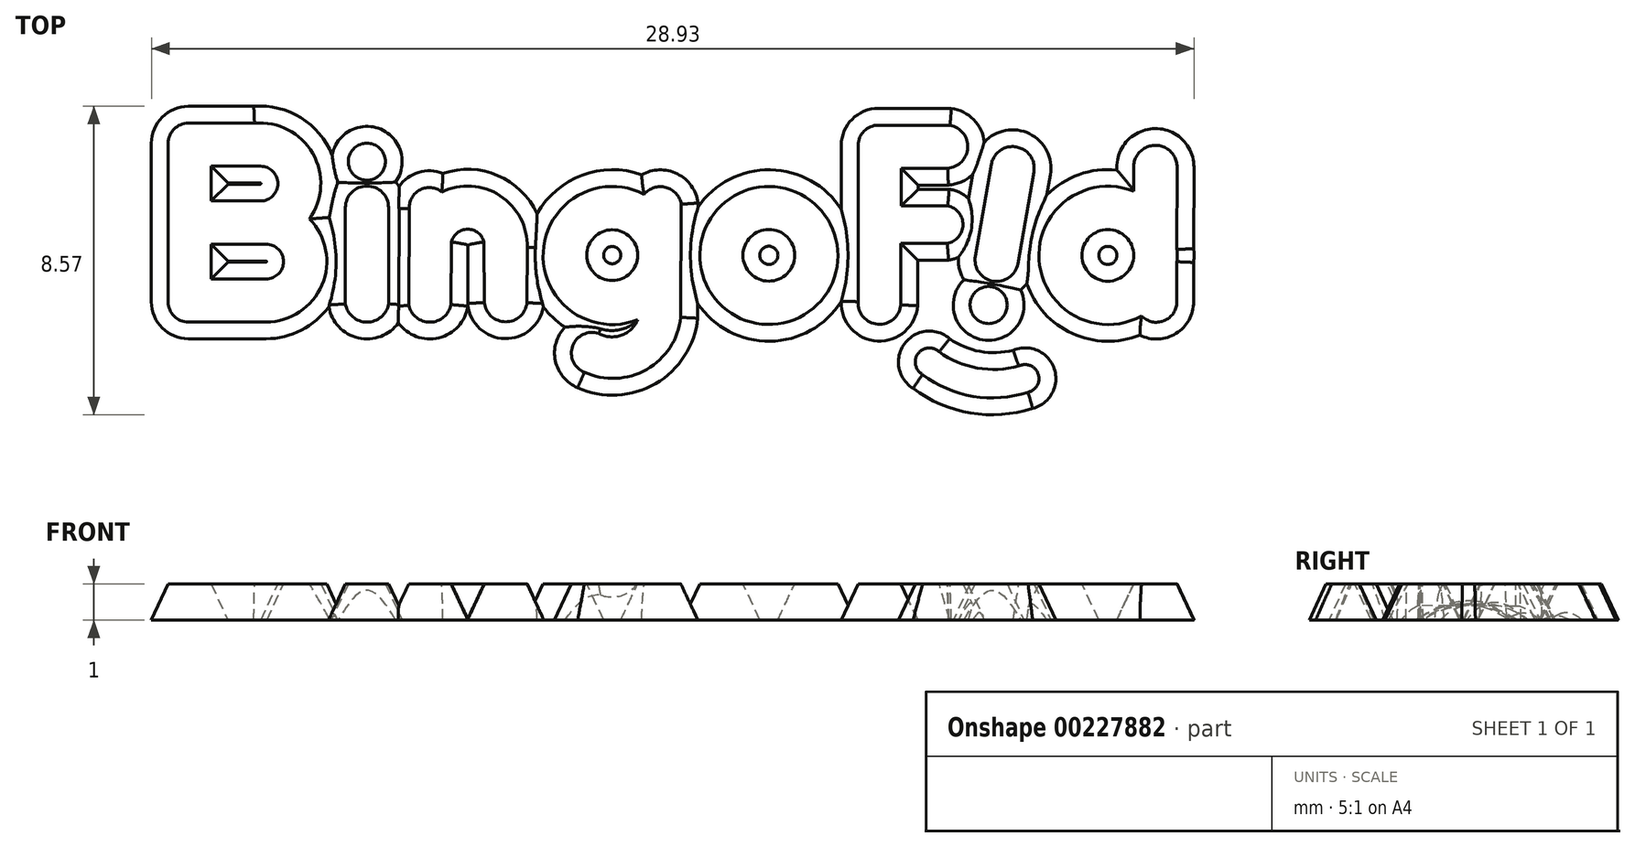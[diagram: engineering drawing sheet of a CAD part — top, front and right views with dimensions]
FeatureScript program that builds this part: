
annotation { "Feature Type Name" : "Feature", "Feature Type Description" : "" }
export const myFeature = defineFeature(function(context is Context, id is Id, definition is map)
    precondition{}
    {
        {
            var Q0;
            Q0=qCreatedBy(makeId("Top.planeOp"),FACE);
            var sketch = newSketch(context, id + "F0", { "sketchPlane" : qUnion([Q0])});
            skArc(sketch, "E0.0.0", {"start": v(-138.67, -42.82) * mm, "mid": v(-138.58, -41) * mm, "end": v(-140.2, -40.16) * mm});
            skLineSegment(sketch, "E0.0.1", {"start": v(-140.2, -40.16) * mm, "end": v(-142.04, -40.16) * mm});
            skArc(sketch, "E0.0.2", {"start": v(-142.04, -40.16) * mm, "mid": v(-142.43, -40.32) * mm, "end": v(-142.6, -40.72) * mm});
            skLineSegment(sketch, "E0.0.3", {"start": v(-142.6, -40.72) * mm, "end": v(-142.6, -45.12) * mm});
            skArc(sketch, "E0.0.4", {"start": v(-142.6, -45.12) * mm, "mid": v(-142.43, -45.52) * mm, "end": v(-142.04, -45.68) * mm});
            skLineSegment(sketch, "E0.0.5", {"start": v(-142.04, -45.68) * mm, "end": v(-139.88, -45.68) * mm});
            skArc(sketch, "E0.0.6", {"start": v(-139.88, -45.68) * mm, "mid": v(-138.33, -44.65) * mm, "end": v(-138.67, -42.82) * mm});
            skArc(sketch, "E1.0.0", {"start": v(-136.48, -42.5) * mm, "mid": v(-137.08, -41.9) * mm, "end": v(-137.68, -42.5) * mm});
            skLineSegment(sketch, "E1.0.1", {"start": v(-137.68, -42.5) * mm, "end": v(-137.68, -45.18) * mm});
            skArc(sketch, "E1.0.2", {"start": v(-137.68, -45.18) * mm, "mid": v(-137.08, -45.69) * mm, "end": v(-136.48, -45.18) * mm});
            skLineSegment(sketch, "E1.0.3", {"start": v(-136.48, -45.18) * mm, "end": v(-136.48, -42.5) * mm});
            skCircle(sketch, "E2.0.0", {"center": v(-137.08, -41.23) * mm, "radius": 0.51 * mm});
            skArc(sketch, "E3.0.0", {"start": v(-135, -42.07) * mm, "mid": v(-135.6, -42) * mm, "end": v(-135.9, -42.53) * mm});
            skLineSegment(sketch, "E3.0.1", {"start": v(-135.9, -42.53) * mm, "end": v(-135.92, -45.22) * mm});
            skArc(sketch, "E3.0.2", {"start": v(-135.92, -45.22) * mm, "mid": v(-135.33, -45.69) * mm, "end": v(-134.75, -45.2) * mm});
            skLineSegment(sketch, "E3.0.3", {"start": v(-134.75, -45.2) * mm, "end": v(-134.73, -43.46) * mm});
            skArc(sketch, "E3.0.4", {"start": v(-134.73, -43.46) * mm, "mid": v(-134.28, -43.1) * mm, "end": v(-133.83, -43.46) * mm});
            skLineSegment(sketch, "E3.0.5", {"start": v(-133.83, -43.46) * mm, "end": v(-133.82, -45.14) * mm});
            skArc(sketch, "E3.0.6", {"start": v(-133.82, -45.14) * mm, "mid": v(-133.23, -45.68) * mm, "end": v(-132.64, -45.15) * mm});
            skLineSegment(sketch, "E3.0.7", {"start": v(-132.64, -45.15) * mm, "end": v(-132.63, -43.62) * mm});
            skArc(sketch, "E3.0.8", {"start": v(-132.63, -43.62) * mm, "mid": v(-133.38, -42.18) * mm, "end": v(-135, -42.07) * mm});
            skArc(sketch, "E4.0.0", {"start": v(-128.36, -42.41) * mm, "mid": v(-128.78, -41.94) * mm, "end": v(-129.39, -42.14) * mm});
            skArc(sketch, "E4.0.1", {"start": v(-129.39, -42.14) * mm, "mid": v(-132.19, -43.74) * mm, "end": v(-129.57, -45.62) * mm});
            skArc(sketch, "E4.0.2", {"start": v(-129.57, -45.62) * mm, "mid": v(-130.02, -46.05) * mm, "end": v(-130.65, -46) * mm});
            skArc(sketch, "E4.0.3", {"start": v(-130.65, -46) * mm, "mid": v(-131.37, -46.35) * mm, "end": v(-131.05, -47.08) * mm});
            skArc(sketch, "E4.0.4", {"start": v(-131.05, -47.08) * mm, "mid": v(-129.32, -47) * mm, "end": v(-128.37, -45.55) * mm});
            skLineSegment(sketch, "E4.0.5", {"start": v(-128.37, -45.55) * mm, "end": v(-128.36, -42.41) * mm});
            skCircle(sketch, "E5.0.0", {"center": v(-125.93, -43.84) * mm, "radius": 1.92 * mm});
            skArc(sketch, "E6.0.0", {"start": v(-120.98, -43.5) * mm, "mid": v(-120.54, -42.98) * mm, "end": v(-120.96, -42.46) * mm});
            skLineSegment(sketch, "E6.0.1", {"start": v(-120.96, -42.46) * mm, "end": v(-122.26, -42.46) * mm});
            skLineSegment(sketch, "E6.0.2", {"start": v(-122.26, -42.46) * mm, "end": v(-122.26, -42.46) * mm});
            skFitSpline(sketch, "E6.0.3", {"points": [v(-122.26, -42.46) * mm, v(-122.26, -42.1) * mm, v(-122.26, -41.76) * mm, v(-122.26, -41.41) * mm]});
            skFitSpline(sketch, "E6.0.4", {"points": [v(-122.26, -41.41) * mm, v(-122.03, -41.41) * mm, v(-121.8, -41.41) * mm, v(-121.58, -41.41) * mm]});
            skLineSegment(sketch, "E6.0.5", {"start": v(-121.58, -41.41) * mm, "end": v(-120.96, -41.41) * mm});
            skArc(sketch, "E6.0.6", {"start": v(-120.96, -41.41) * mm, "mid": v(-120.4, -40.84) * mm, "end": v(-120.9, -40.22) * mm});
            skLineSegment(sketch, "E6.0.7", {"start": v(-120.9, -40.22) * mm, "end": v(-122.9, -40.22) * mm});
            skArc(sketch, "E6.0.8", {"start": v(-122.9, -40.22) * mm, "mid": v(-123.29, -40.38) * mm, "end": v(-123.45, -40.78) * mm});
            skLineSegment(sketch, "E6.0.9", {"start": v(-123.45, -40.78) * mm, "end": v(-123.45, -45.12) * mm});
            skArc(sketch, "E6.0.10", {"start": v(-123.45, -45.12) * mm, "mid": v(-122.9, -45.75) * mm, "end": v(-122.27, -45.21) * mm});
            skLineSegment(sketch, "E6.0.11", {"start": v(-122.27, -45.21) * mm, "end": v(-122.27, -43.5) * mm});
            skLineSegment(sketch, "E6.0.12", {"start": v(-122.27, -43.5) * mm, "end": v(-120.98, -43.5) * mm});
            skArc(sketch, "E7.0.0", {"start": v(-120.2, -43.86) * mm, "mid": v(-119.71, -44.55) * mm, "end": v(-119.02, -44.06) * mm});
            skLineSegment(sketch, "E7.0.1", {"start": v(-119.02, -44.06) * mm, "end": v(-118.57, -41.51) * mm});
            skArc(sketch, "E7.0.2", {"start": v(-118.57, -41.51) * mm, "mid": v(-119.06, -40.82) * mm, "end": v(-119.75, -41.3) * mm});
            skLineSegment(sketch, "E7.0.3", {"start": v(-119.75, -41.3) * mm, "end": v(-120.2, -43.86) * mm});
            skCircle(sketch, "E8.0.0", {"center": v(-119.83, -45.21) * mm, "radius": 0.52 * mm});
            skArc(sketch, "E9.0.0", {"start": v(-121.2, -46.51) * mm, "mid": v(-121.79, -46.57) * mm, "end": v(-121.66, -47.14) * mm});
            skArc(sketch, "E9.0.1", {"start": v(-121.66, -47.14) * mm, "mid": v(-120.26, -47.75) * mm, "end": v(-118.73, -47.63) * mm});
            skArc(sketch, "E9.0.2", {"start": v(-118.73, -47.63) * mm, "mid": v(-118.45, -47.13) * mm, "end": v(-119, -46.9) * mm});
            skArc(sketch, "E9.0.3", {"start": v(-119, -46.9) * mm, "mid": v(-120.14, -46.96) * mm, "end": v(-121.2, -46.51) * mm});
            skLineSegment(sketch, "E10.0.0", {"start": v(-115.8, -41.39) * mm, "end": v(-115.8, -42.05) * mm});
            skArc(sketch, "E10.0.1", {"start": v(-115.8, -42.05) * mm, "mid": v(-118.43, -43.95) * mm, "end": v(-115.59, -45.51) * mm});
            skArc(sketch, "E10.0.2", {"start": v(-115.59, -45.51) * mm, "mid": v(-114.96, -45.65) * mm, "end": v(-114.6, -45.12) * mm});
            skLineSegment(sketch, "E10.0.3", {"start": v(-114.6, -45.12) * mm, "end": v(-114.6, -44) * mm});
            skArc(sketch, "E10.0.4", {"start": v(-114.6, -44) * mm, "mid": v(-114.6, -43.84) * mm, "end": v(-114.6, -43.67) * mm});
            skLineSegment(sketch, "E10.0.5", {"start": v(-114.6, -43.67) * mm, "end": v(-114.6, -41.38) * mm});
            skArc(sketch, "E10.0.6", {"start": v(-114.6, -41.38) * mm, "mid": v(-115.2, -40.78) * mm, "end": v(-115.8, -41.39) * mm});
            skArc(sketch, "E11.0", {"start": v(-140.03, -42.32) * mm, "mid": v(-139.55, -41.84) * mm, "end": v(-140.03, -41.36) * mm});
            skFitSpline(sketch, "E12.0", {"points": [v(-141.4, -42.32) * mm, v(-141.4, -42) * mm, v(-141.4, -41.68) * mm, v(-141.4, -41.36) * mm]});
            skFitSpline(sketch, "E12.1", {"points": [v(-141.4, -44.49) * mm, v(-141.4, -44.17) * mm, v(-141.4, -43.84) * mm, v(-141.4, -43.52) * mm]});
            skArc(sketch, "E12.2", {"start": v(-139.88, -44.49) * mm, "mid": v(-139.4, -44) * mm, "end": v(-139.88, -43.52) * mm});
            skCircle(sketch, "E13.0", {"center": v(-130.27, -43.83) * mm, "radius": 0.7 * mm});
            skCircle(sketch, "E14.0", {"center": v(-125.93, -43.83) * mm, "radius": 0.72 * mm});
            skCircle(sketch, "E15.0", {"center": v(-116.52, -43.83) * mm, "radius": 0.72 * mm});
            skLineSegment(sketch, "E16", {"start": v(-141.4, -41.36) * mm, "end": v(-140.03, -41.36) * mm});
            skLineSegment(sketch, "E17", {"start": v(-141.4, -42.32) * mm, "end": v(-140.03, -42.32) * mm});
            skLineSegment(sketch, "E18", {"start": v(-141.4, -43.52) * mm, "end": v(-139.88, -43.52) * mm});
            skLineSegment(sketch, "E19", {"start": v(-141.4, -44.49) * mm, "end": v(-139.88, -44.49) * mm});
            skSolve(sketch);
        }
        {
            var Q0;
            Q0=makeQuery(id+"F0.imprint","IMPRINT",FACE,{"disambiguationData":[TD([[makeQuery(id+"F0.imprint","IMPRINT",EDGE,{"derivedFrom":sQuery(id+"F0.wireOp",EDGE,"E0.0.0")}),1.0]])]});
            var Q1;
            Q1=makeQuery(id+"F0.imprint","IMPRINT",FACE,{"disambiguationData":[TD([[makeQuery(id+"F0.imprint","IMPRINT",EDGE,{"derivedFrom":sQuery(id+"F0.wireOp",EDGE,"E1.0.0")}),1.0]])]});
            var Q2;
            Q2=makeQuery(id+"F0.imprint","IMPRINT",FACE,{"disambiguationData":[TD([[makeQuery(id+"F0.imprint","IMPRINT",EDGE,{"derivedFrom":sQuery(id+"F0.wireOp",EDGE,"E2.0.0")}),1.0]])]});
            var Q3;
            Q3=makeQuery(id+"F0.imprint","IMPRINT",FACE,{"disambiguationData":[TD([[makeQuery(id+"F0.imprint","IMPRINT",EDGE,{"derivedFrom":sQuery(id+"F0.wireOp",EDGE,"E3.0.0")}),1.0]])]});
            var Q4;
            Q4=makeQuery(id+"F0.imprint","IMPRINT",FACE,{"disambiguationData":[TD([[makeQuery(id+"F0.imprint","IMPRINT",EDGE,{"derivedFrom":sQuery(id+"F0.wireOp",EDGE,"E4.0.0")}),1.0]])]});
            var Q5;
            Q5=makeQuery(id+"F0.imprint","IMPRINT",FACE,{"disambiguationData":[TD([[makeQuery(id+"F0.imprint","IMPRINT",EDGE,{"derivedFrom":sQuery(id+"F0.wireOp",EDGE,"E5.0.0")}),1.0]])]});
            var Q6;
            Q6=makeQuery(id+"F0.imprint","IMPRINT",FACE,{"disambiguationData":[TD([[makeQuery(id+"F0.imprint","IMPRINT",EDGE,{"derivedFrom":sQuery(id+"F0.wireOp",EDGE,"E6.0.0")}),1.0]])]});
            var Q7;
            Q7=makeQuery(id+"F0.imprint","IMPRINT",FACE,{"disambiguationData":[TD([[makeQuery(id+"F0.imprint","IMPRINT",EDGE,{"derivedFrom":sQuery(id+"F0.wireOp",EDGE,"E7.0.0")}),1.0]])]});
            var Q8;
            Q8=makeQuery(id+"F0.imprint","IMPRINT",FACE,{"disambiguationData":[TD([[makeQuery(id+"F0.imprint","IMPRINT",EDGE,{"derivedFrom":sQuery(id+"F0.wireOp",EDGE,"E10.0.0")}),1.0]])]});
            var Q9;
            Q9=makeQuery(id+"F0.imprint","IMPRINT",FACE,{"disambiguationData":[TD([[makeQuery(id+"F0.imprint","IMPRINT",EDGE,{"derivedFrom":sQuery(id+"F0.wireOp",EDGE,"E8.0.0")}),1.0]])]});
            var Q10;
            Q10=makeQuery(id+"F0.imprint","IMPRINT",FACE,{"disambiguationData":[TD([[makeQuery(id+"F0.imprint","IMPRINT",EDGE,{"derivedFrom":sQuery(id+"F0.wireOp",EDGE,"E9.0.0")}),1.0]])]});
            extrude(context, id + "F1", {"entities" : qUnion([Q0, Q1, Q2, Q3, Q4, Q5, Q6, Q7, Q8, Q9, Q10]), "oppositeDirection" : true, "depth" : 1 * mm, "hasDraft" : true, "draftAngle" : 25 * degree});
        }
        {
            var Q0;
            Q0=makeQuery(id+"F1.opExtrude","SWEPT_BODY",BODY,{"disambiguationData":[OSD([sQuery(id+"F0.wireOp",EDGE,"E10.0.0"),sQuery(id+"F0.wireOp",EDGE,"E10.0.1"),sQuery(id+"F0.wireOp",EDGE,"E10.0.2"),sQuery(id+"F0.wireOp",EDGE,"E10.0.3"),sQuery(id+"F0.wireOp",EDGE,"E10.0.4"),sQuery(id+"F0.wireOp",EDGE,"E10.0.5"),sQuery(id+"F0.wireOp",EDGE,"E10.0.6"),sQuery(id+"F0.wireOp",EDGE,"E15.0")])]});
            var Q1;
            Q1=makeQuery(id+"F1.opExtrude","SWEPT_BODY",BODY,{"disambiguationData":[OSD([sQuery(id+"F0.wireOp",EDGE,"E0.0.0"),sQuery(id+"F0.wireOp",EDGE,"E0.0.1"),sQuery(id+"F0.wireOp",EDGE,"E0.0.2"),sQuery(id+"F0.wireOp",EDGE,"E0.0.3"),sQuery(id+"F0.wireOp",EDGE,"E0.0.4"),sQuery(id+"F0.wireOp",EDGE,"E0.0.5"),sQuery(id+"F0.wireOp",EDGE,"E0.0.6"),sQuery(id+"F0.wireOp",EDGE,"E11.0"),sQuery(id+"F0.wireOp",EDGE,"E12.0"),sQuery(id+"F0.wireOp",EDGE,"E12.1"),sQuery(id+"F0.wireOp",EDGE,"E12.2"),sQuery(id+"F0.wireOp",EDGE,"E16"),sQuery(id+"F0.wireOp",EDGE,"E17"),sQuery(id+"F0.wireOp",EDGE,"E18"),sQuery(id+"F0.wireOp",EDGE,"E19")])]});
            var Q2;
            Q2=makeQuery(id+"F1.opExtrude","SWEPT_BODY",BODY,{"disambiguationData":[OSD([sQuery(id+"F0.wireOp",EDGE,"E2.0.0")])]});
            var Q3;
            Q3=makeQuery(id+"F1.opExtrude","SWEPT_BODY",BODY,{"disambiguationData":[OSD([sQuery(id+"F0.wireOp",EDGE,"E1.0.0"),sQuery(id+"F0.wireOp",EDGE,"E1.0.1"),sQuery(id+"F0.wireOp",EDGE,"E1.0.2"),sQuery(id+"F0.wireOp",EDGE,"E1.0.3")])]});
            var Q4;
            Q4=makeQuery(id+"F1.opExtrude","SWEPT_BODY",BODY,{"disambiguationData":[OSD([sQuery(id+"F0.wireOp",EDGE,"E3.0.0"),sQuery(id+"F0.wireOp",EDGE,"E3.0.1"),sQuery(id+"F0.wireOp",EDGE,"E3.0.2"),sQuery(id+"F0.wireOp",EDGE,"E3.0.3"),sQuery(id+"F0.wireOp",EDGE,"E3.0.4"),sQuery(id+"F0.wireOp",EDGE,"E3.0.5"),sQuery(id+"F0.wireOp",EDGE,"E3.0.6"),sQuery(id+"F0.wireOp",EDGE,"E3.0.7"),sQuery(id+"F0.wireOp",EDGE,"E3.0.8")])]});
            var Q5;
            Q5=makeQuery(id+"F1.opExtrude","SWEPT_BODY",BODY,{"disambiguationData":[OSD([sQuery(id+"F0.wireOp",EDGE,"E4.0.0"),sQuery(id+"F0.wireOp",EDGE,"E4.0.1"),sQuery(id+"F0.wireOp",EDGE,"E4.0.2"),sQuery(id+"F0.wireOp",EDGE,"E4.0.3"),sQuery(id+"F0.wireOp",EDGE,"E4.0.4"),sQuery(id+"F0.wireOp",EDGE,"E4.0.5"),sQuery(id+"F0.wireOp",EDGE,"E13.0")])]});
            var Q6;
            Q6=makeQuery(id+"F1.opExtrude","SWEPT_BODY",BODY,{"disambiguationData":[OSD([sQuery(id+"F0.wireOp",EDGE,"E5.0.0"),sQuery(id+"F0.wireOp",EDGE,"E14.0")])]});
            var Q7;
            Q7=makeQuery(id+"F1.opExtrude","SWEPT_BODY",BODY,{"disambiguationData":[OSD([sQuery(id+"F0.wireOp",EDGE,"E6.0.0"),sQuery(id+"F0.wireOp",EDGE,"E6.0.1"),sQuery(id+"F0.wireOp",EDGE,"E6.0.2"),sQuery(id+"F0.wireOp",EDGE,"E6.0.3"),sQuery(id+"F0.wireOp",EDGE,"E6.0.4"),sQuery(id+"F0.wireOp",EDGE,"E6.0.5"),sQuery(id+"F0.wireOp",EDGE,"E6.0.6"),sQuery(id+"F0.wireOp",EDGE,"E6.0.7"),sQuery(id+"F0.wireOp",EDGE,"E6.0.8"),sQuery(id+"F0.wireOp",EDGE,"E6.0.9"),sQuery(id+"F0.wireOp",EDGE,"E6.0.10"),sQuery(id+"F0.wireOp",EDGE,"E6.0.11"),sQuery(id+"F0.wireOp",EDGE,"E6.0.12")])]});
            var Q8;
            Q8=makeQuery(id+"F1.opExtrude","SWEPT_BODY",BODY,{"disambiguationData":[OSD([sQuery(id+"F0.wireOp",EDGE,"E9.0.0"),sQuery(id+"F0.wireOp",EDGE,"E9.0.1"),sQuery(id+"F0.wireOp",EDGE,"E9.0.2"),sQuery(id+"F0.wireOp",EDGE,"E9.0.3")])]});
            var Q9;
            Q9=makeQuery(id+"F1.opExtrude","SWEPT_BODY",BODY,{"disambiguationData":[OSD([sQuery(id+"F0.wireOp",EDGE,"E8.0.0")])]});
            var Q10;
            Q10=makeQuery(id+"F1.opExtrude","SWEPT_BODY",BODY,{"disambiguationData":[OSD([sQuery(id+"F0.wireOp",EDGE,"E7.0.0"),sQuery(id+"F0.wireOp",EDGE,"E7.0.1"),sQuery(id+"F0.wireOp",EDGE,"E7.0.2"),sQuery(id+"F0.wireOp",EDGE,"E7.0.3")])]});
            booleanBodies(context, id + "F2", {"operationType" : BooleanOperationType.UNION, "tools" : qUnion([Q0, Q1, Q2, Q3, Q4, Q5, Q6, Q7, Q8, Q9, Q10])});
        }
    });
